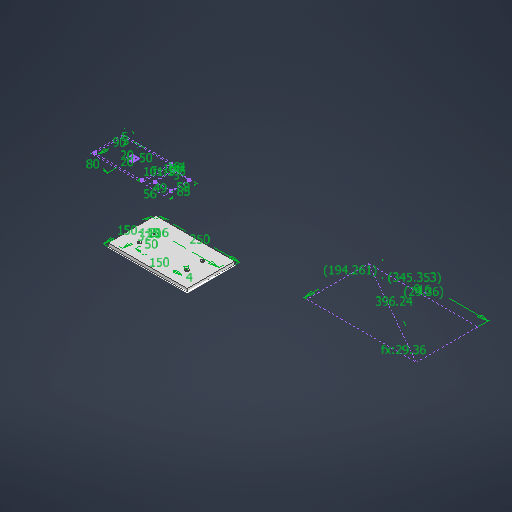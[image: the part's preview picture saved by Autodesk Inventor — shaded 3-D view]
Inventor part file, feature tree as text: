
AUTODESK INVENTOR PART (.ipt)
format: ipt  version: 2025.1 (Build 291241000, 241)  size: 260,096 bytes
history: native  units: mm
features: extrude x2, sketch x1
ambient origin geometry x8: Origin, YZ Plane, XZ Plane, XY Plane, X Axis, Y Axis, Z Axis, Center Point
bodies: Body1 (feature_tree)
feature tree (3):
  sketch  "Sketch1"  dims[d0=150.0mm d1=50.0mm d2=4.0mm d3=32.0mm d4=216.0mm d5=115.0mm d34=396.24mm d37=345.353091mm d39=9.0mm d40=16.0mm d41=5.123895mm d42=5.123895mm d43=194.261114mm d46=161.0mm d47=101.0mm d48=3.0mm d49=150.0mm d50=90.0mm d51=5.0mm d52=20.0mm d53=20.0mm d54=50.0mm d55=80.0mm d56=56.0mm d57=85.0mm d58=49.0mm d59=58.0mm d60=3.0mm d61=3.5mm d62=15.0mm d63=15.0mm d64=250.0mm d65=150.0mm d66=10.0mm d69=10.0mm d70=0.0mm d71=2.0mm d72=0.0mm]
  extrude  "Extrusion2"  Depth=2.0mm
  extrude  "Extrusion3"  Depth=2.0mm
